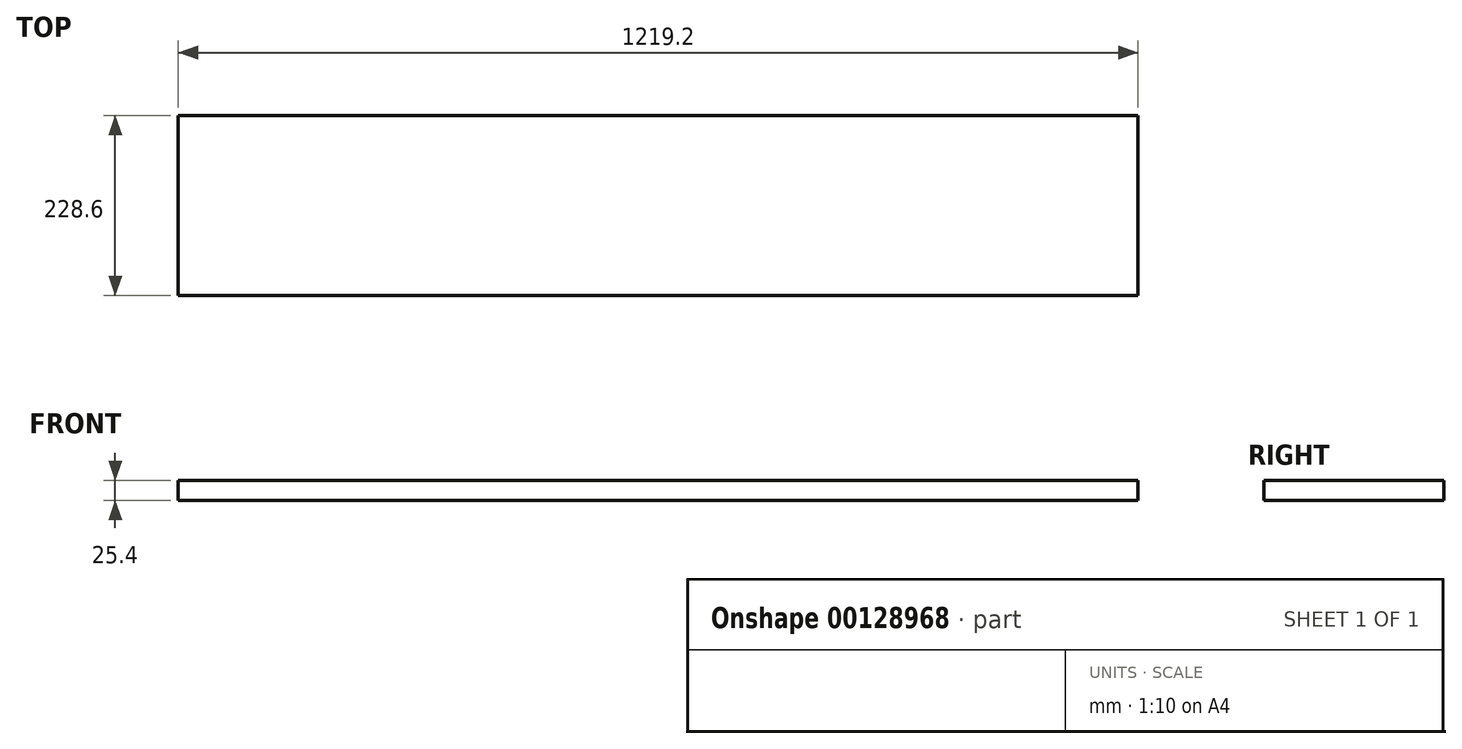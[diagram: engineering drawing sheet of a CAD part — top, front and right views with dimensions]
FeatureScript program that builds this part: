
annotation { "Feature Type Name" : "Feature", "Feature Type Description" : "" }
export const myFeature = defineFeature(function(context is Context, id is Id, definition is map)
    precondition{}
    {
        {
            var Q0;
            Q0=qCreatedBy(makeId("Top.planeOp"),FACE);
            var sketch = newSketch(context, id + "F0", { "sketchPlane" : qUnion([Q0])});
            skLineSegment(sketch, "E0.bottom", {"start": v(0, 0) * mm, "end": v(-1219.2, 0) * mm});
            skLineSegment(sketch, "E0.top", {"start": v(0, 228.6) * mm, "end": v(-1219.2, 228.6) * mm});
            skLineSegment(sketch, "E0.left", {"start": v(0, 0) * mm, "end": v(0, 228.6) * mm});
            skLineSegment(sketch, "E0.right", {"start": v(-1219.2, 0) * mm, "end": v(-1219.2, 228.6) * mm});
            skSolve(sketch);
        }
        {
            var Q0;
            Q0=qSketchRegion(id+"F0",true);
            extrude(context, id + "F1", {"entities" : qUnion([Q0]), "depth" : 25.4 * mm});
        }
    });
